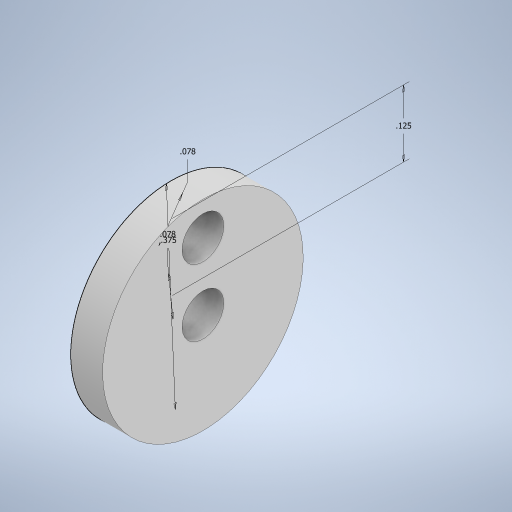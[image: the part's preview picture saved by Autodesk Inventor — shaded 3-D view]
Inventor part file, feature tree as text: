
AUTODESK INVENTOR PART (.ipt)
format: ipt  version: 2023 (Build 270158000, 158)  size: 233,984 bytes
history: native  units: in
note: dims shown in document units (in); Inventor stores cm internally (conversion verified against a paired STEP export)
features: extrude x1, sketch x1
ambient origin geometry x8: Origin, YZ Plane, XZ Plane, XY Plane, X Axis, Y Axis, Z Axis, Center Point
bodies: Solid1 (feature_tree)
feature tree (2):
  extrude  "Extrusion1"  Depth=0.06in
  sketch  "Sketch1"  dims[d0=0.375in d1=0.0781in d2=0.125in d3=0.0781in d4=0.06in d5=0.0in]
